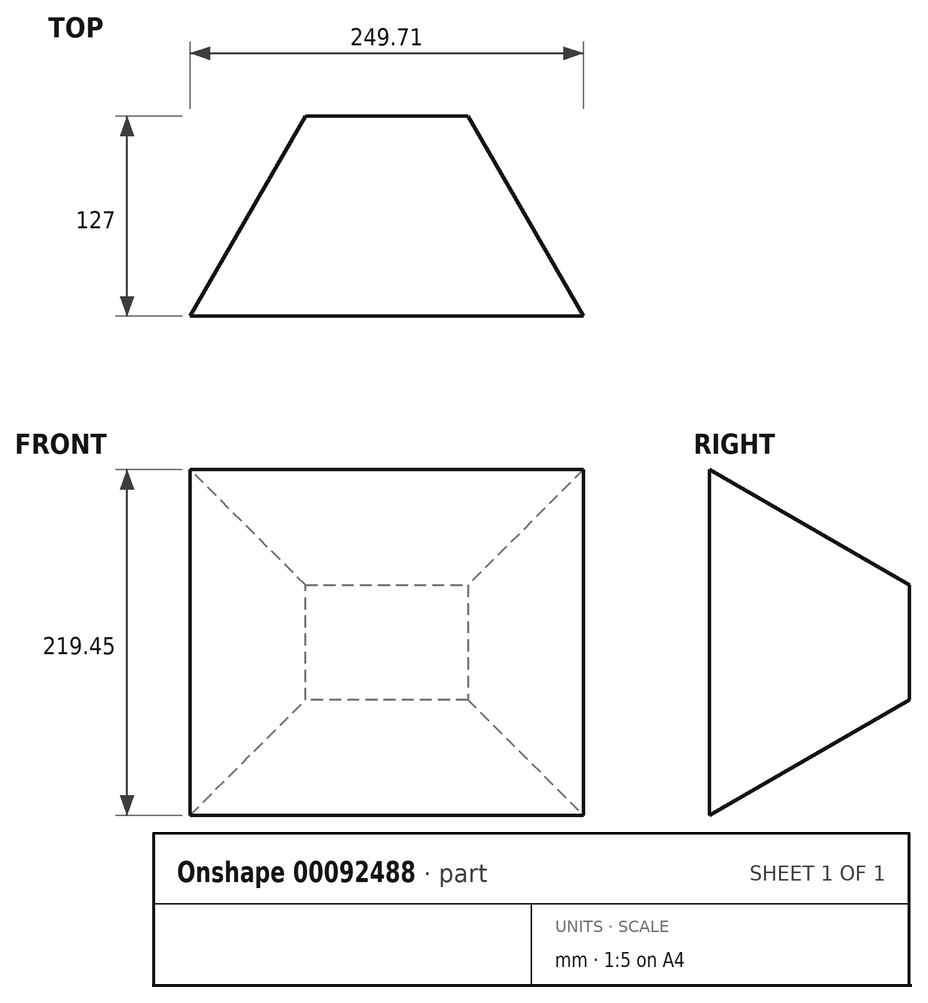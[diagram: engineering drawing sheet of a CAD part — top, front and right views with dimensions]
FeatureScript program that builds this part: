
annotation { "Feature Type Name" : "Feature", "Feature Type Description" : "" }
export const myFeature = defineFeature(function(context is Context, id is Id, definition is map)
    precondition{}
    {
        {
            var Q0;
            Q0=qCreatedBy(makeId("Front.planeOp"),FACE);
            var sketch = newSketch(context, id + "F0", { "sketchPlane" : qUnion([Q0])});
            skLineSegment(sketch, "E0.bottom", {"start": v(-58.67, 51.17) * mm, "end": v(44.39, 51.17) * mm});
            skLineSegment(sketch, "E0.top", {"start": v(-58.67, -21.63) * mm, "end": v(44.39, -21.63) * mm});
            skLineSegment(sketch, "E0.left", {"start": v(-58.67, 51.17) * mm, "end": v(-58.67, -21.63) * mm});
            skLineSegment(sketch, "E0.right", {"start": v(44.39, 51.17) * mm, "end": v(44.39, -21.63) * mm});
            skSolve(sketch);
        }
        {
            var Q0;
            Q0=makeQuery(id+"F0.imprint","IMPRINT",FACE,{"disambiguationData":[TD([[makeQuery(id+"F0.imprint","IMPRINT",EDGE,{"derivedFrom":sQuery(id+"F0.wireOp",EDGE,"E0.bottom")}),-1.0]])]});
            extrude(context, id + "F1", {"entities" : qUnion([Q0]), "depth" : 127 * mm, "hasDraft" : true, "draftAngle" : 30 * degree});
        }
    });
